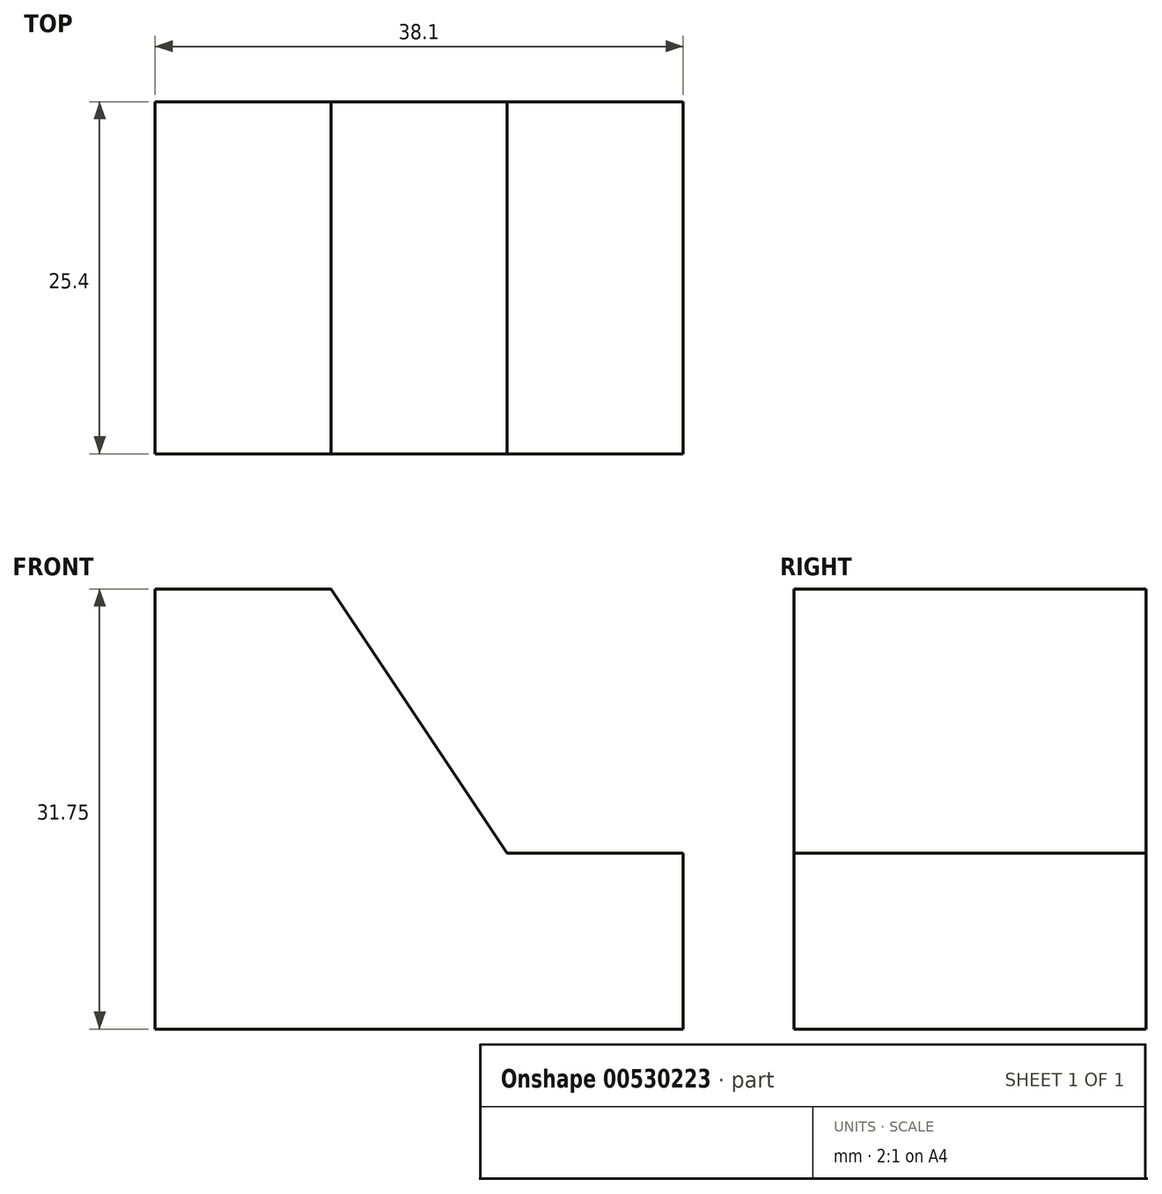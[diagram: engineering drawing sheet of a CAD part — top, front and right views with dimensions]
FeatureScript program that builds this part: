
annotation { "Feature Type Name" : "Feature", "Feature Type Description" : "" }
export const myFeature = defineFeature(function(context is Context, id is Id, definition is map)
    precondition{}
    {
        {
            var Q0;
            Q0=qCreatedBy(makeId("Right.planeOp"),FACE);
            var sketch = newSketch(context, id + "F0", { "sketchPlane" : qUnion([Q0])});
            skLineSegment(sketch, "E0", {"start": v(0, 0) * mm, "end": v(25.4, 0) * mm});
            skLineSegment(sketch, "E1", {"start": v(25.4, 0) * mm, "end": v(25.4, 12.7) * mm});
            skLineSegment(sketch, "E2", {"start": v(25.4, 12.7) * mm, "end": v(0, 12.7) * mm});
            skLineSegment(sketch, "E3", {"start": v(0, 12.7) * mm, "end": v(0, 0) * mm});
            skSolve(sketch);
        }
        {
            var Q0;
            Q0=makeQuery(id+"F0.imprint","IMPRINT",FACE,{"disambiguationData":[TD([[makeQuery(id+"F0.imprint","IMPRINT",EDGE,{"derivedFrom":sQuery(id+"F0.wireOp",EDGE,"E0")}),1.0]])]});
            extrude(context, id + "F1", {"entities" : qUnion([Q0]), "depth" : 38.1 * mm, "offsetDistance" : 25.4 * mm});
        }
        {
            var Q0;
            Q0=makeQuery(id+"F1.opExtrude","SWEPT_FACE",FACE,{"disambiguationData":[OSD([sQuery(id+"F0.wireOp",EDGE,"E3")])]});
            var sketch = newSketch(context, id + "F2", { "sketchPlane" : qUnion([Q0])});
            skLineSegment(sketch, "E4", {"start": v(25.4, 12.7) * mm, "end": v(12.7, 31.75) * mm});
            skLineSegment(sketch, "E5", {"start": v(12.7, 31.75) * mm, "end": v(0, 31.75) * mm});
            skLineSegment(sketch, "E6", {"start": v(0, 31.75) * mm, "end": v(0, 12.7) * mm});
            skLineSegment(sketch, "E7", {"start": v(0, 12.7) * mm, "end": v(25.4, 12.7) * mm});
            skSolve(sketch);
        }
        {
            var Q0;
            Q0=makeQuery(id+"F2.imprint","IMPRINT",FACE,{"disambiguationData":[TD([[makeQuery(id+"F2.imprint","IMPRINT",EDGE,{"derivedFrom":sQuery(id+"F2.wireOp",EDGE,"E4")}),1.0]])]});
            extrude(context, id + "F3", {"entities" : qUnion([Q0]), "operationType" : NewBodyOperationType.ADD, "oppositeDirection" : true, "depth" : 25.4 * mm, "offsetDistance" : 25.4 * mm});
        }
    });
